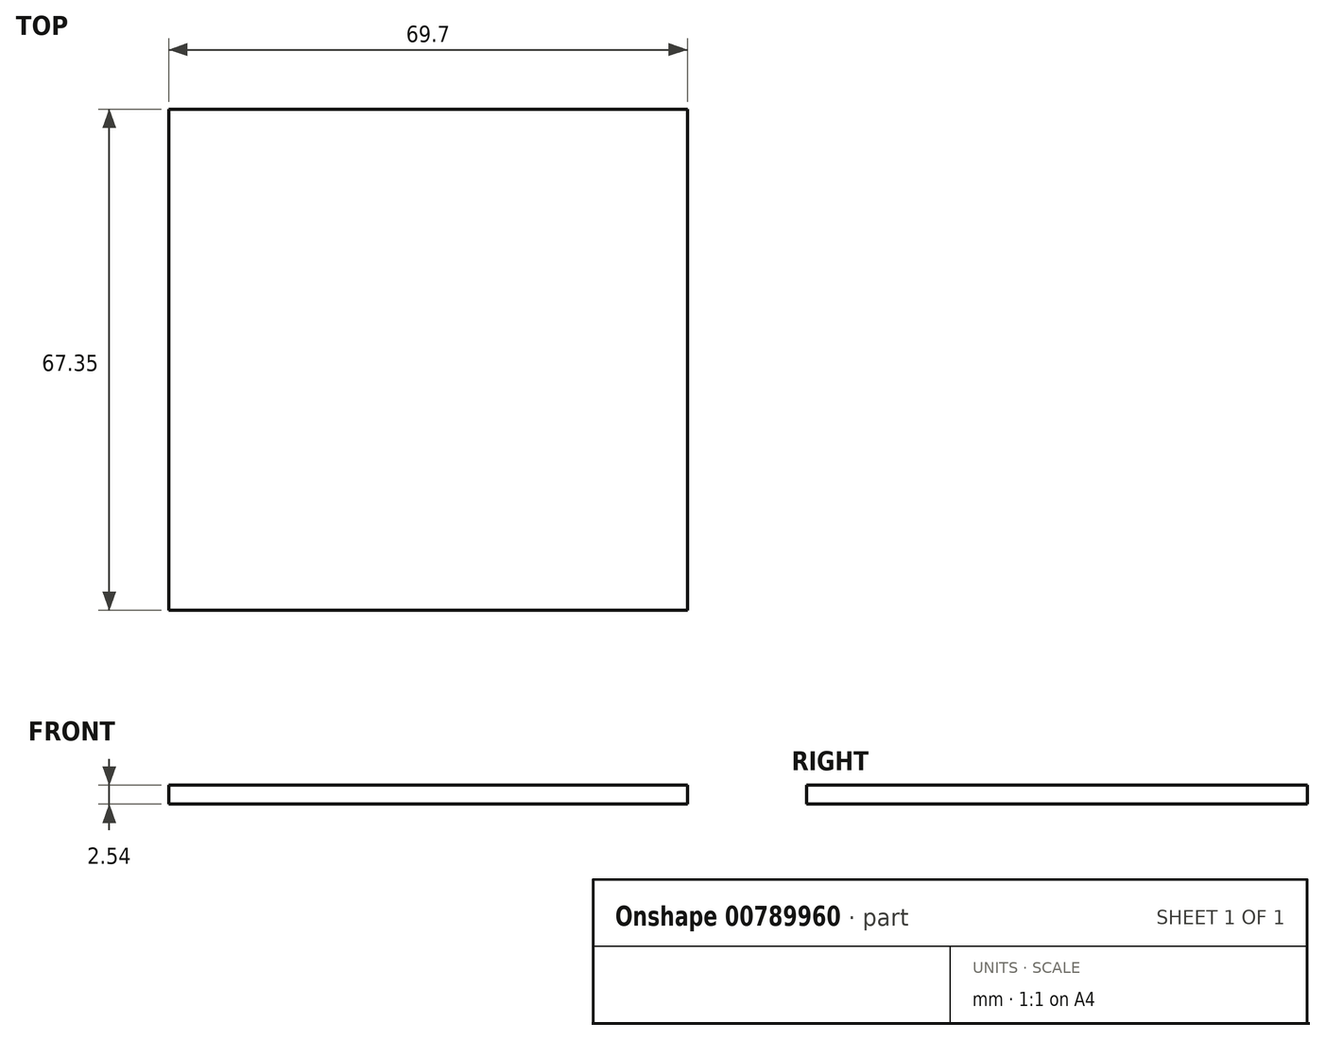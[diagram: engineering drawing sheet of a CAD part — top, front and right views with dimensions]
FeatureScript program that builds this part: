
annotation { "Feature Type Name" : "Feature", "Feature Type Description" : "" }
export const myFeature = defineFeature(function(context is Context, id is Id, definition is map)
    precondition{}
    {
        {
            var Q0;
            Q0=qCreatedBy(makeId("Top.planeOp"),FACE);
            var sketch = newSketch(context, id + "F0", { "sketchPlane" : qUnion([Q0])});
            skLineSegment(sketch, "E0.bottom", {"start": v(0, 0) * mm, "end": v(-69.7, 0) * mm});
            skLineSegment(sketch, "E0.top", {"start": v(0, 67.35) * mm, "end": v(-69.7, 67.35) * mm});
            skLineSegment(sketch, "E0.left", {"start": v(0, 0) * mm, "end": v(0, 67.35) * mm});
            skLineSegment(sketch, "E0.right", {"start": v(-69.7, 0) * mm, "end": v(-69.7, 67.35) * mm});
            skSolve(sketch);
        }
        {
            var Q0;
            Q0=makeQuery(id+"F0.imprint","IMPRINT",FACE,{"disambiguationData":[TD([[makeQuery(id+"F0.imprint","IMPRINT",EDGE,{"derivedFrom":sQuery(id+"F0.wireOp",EDGE,"E0.bottom")}),-1.0]])]});
            extrude(context, id + "F1", {"entities" : qUnion([Q0]), "depth" : 2.54 * mm, "offsetDistance" : 25.4 * mm});
        }
    });
